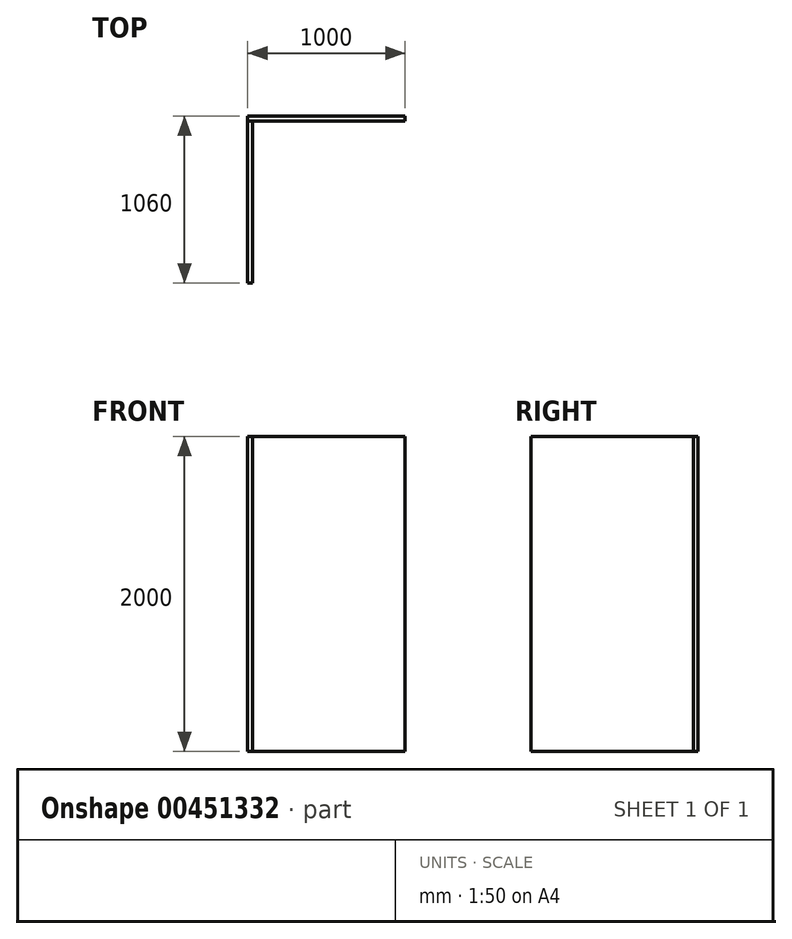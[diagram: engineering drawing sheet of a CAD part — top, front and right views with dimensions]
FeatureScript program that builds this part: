
annotation { "Feature Type Name" : "Feature", "Feature Type Description" : "" }
export const myFeature = defineFeature(function(context is Context, id is Id, definition is map)
    precondition{}
    {
        {
            var Q0;
            Q0=qCreatedBy(makeId("Top.planeOp"),FACE);
            var sketch = newSketch(context, id + "F0", { "sketchPlane" : qUnion([Q0])});
            skLineSegment(sketch, "E0.bottom", {"start": v(0, 0) * mm, "end": v(1000, 0) * mm});
            skLineSegment(sketch, "E0.top", {"start": v(0, 30) * mm, "end": v(1000, 30) * mm});
            skLineSegment(sketch, "E0.left", {"start": v(0, 0) * mm, "end": v(0, 30) * mm});
            skLineSegment(sketch, "E0.right", {"start": v(1000, 0) * mm, "end": v(1000, 30) * mm});
            skLineSegment(sketch, "E1.bottom", {"start": v(0, 0) * mm, "end": v(30, 0) * mm});
            skLineSegment(sketch, "E1.top", {"start": v(0, -1030) * mm, "end": v(30, -1030) * mm});
            skLineSegment(sketch, "E1.left", {"start": v(0, 0) * mm, "end": v(0, -1030) * mm});
            skLineSegment(sketch, "E1.right", {"start": v(30, 0) * mm, "end": v(30, -1030) * mm});
            skSolve(sketch);
        }
        {
            var Q0;
            Q0 = qSketchRegion(id + "F0", true);
            extrude(context, id + "F1", {"entities" : qUnion([Q0]), "depth" : 2000 * mm});
        }
    });
